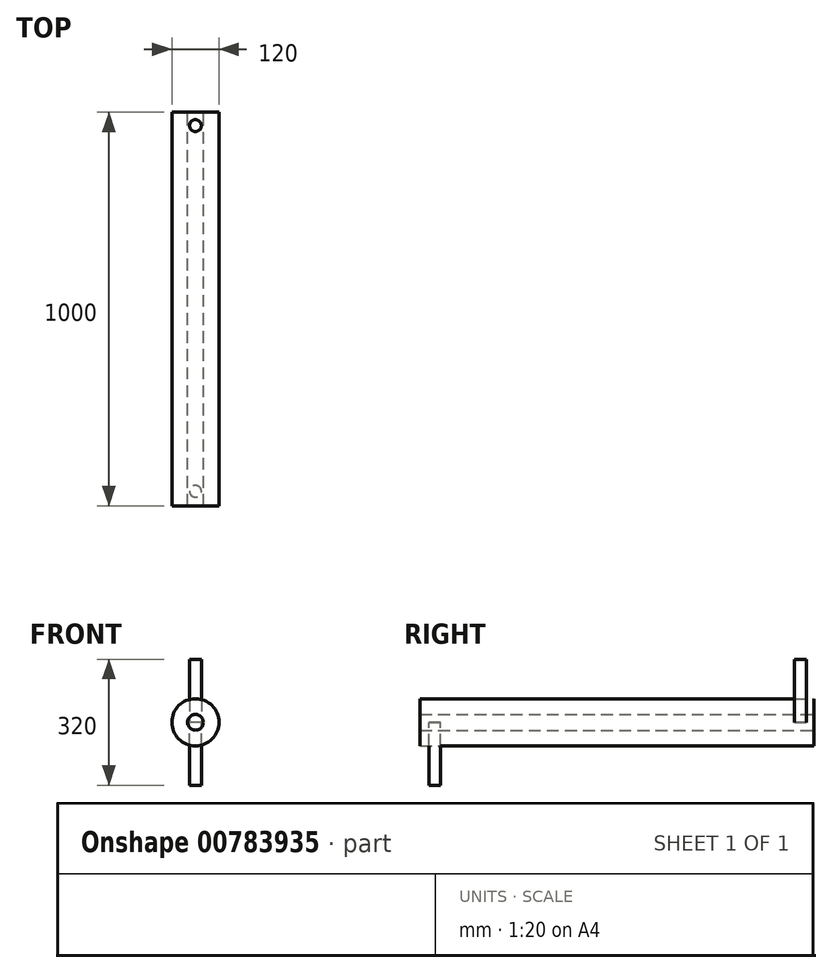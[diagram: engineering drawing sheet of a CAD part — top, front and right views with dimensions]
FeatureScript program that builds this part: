
annotation { "Feature Type Name" : "Feature", "Feature Type Description" : "" }
export const myFeature = defineFeature(function(context is Context, id is Id, definition is map)
    precondition{}
    {
        {
            var Q0;
            Q0=qCreatedBy(makeId("Front.planeOp"),FACE);
            var sketch = newSketch(context, id + "F0", { "sketchPlane" : qUnion([Q0])});
            skCircle(sketch, "E0", {"center": v(0, 0) * mm, "radius": 60 * mm});
            skSolve(sketch);
        }
        {
            var Q0;
            Q0=qCreatedBy(makeId("Front.planeOp"),FACE);
            var sketch = newSketch(context, id + "F1", { "sketchPlane" : qUnion([Q0])});
            skCircle(sketch, "E1", {"center": v(0, 0) * mm, "radius": 20 * mm});
            skSolve(sketch);
        }
        {
            var Q0;
            Q0=makeQuery(id+"F0.imprint","IMPRINT",FACE,{"disambiguationData":[TD([[makeQuery(id+"F0.imprint","IMPRINT",EDGE,{"derivedFrom":sQuery(id+"F0.wireOp",EDGE,"E0")}),1.0]])]});
            var Q1;
            Q1=makeQuery(id+"F1.imprint","IMPRINT",FACE,{"disambiguationData":[TD([[makeQuery(id+"F1.imprint","IMPRINT",EDGE,{"derivedFrom":sQuery(id+"F1.wireOp",EDGE,"E1")}),1.0]])]});
            extrude(context, id + "F2", {"entities" : qUnion([Q0, Q1]), "depth" : 1000 * mm, "offsetDistance" : 25 * mm});
        }
        {
            var Q0;
            Q0=qCreatedBy(makeId("Top.planeOp"),FACE);
            var sketch = newSketch(context, id + "F3", { "sketchPlane" : qUnion([Q0])});
            skCircle(sketch, "E2", {"center": v(0, -33.89) * mm, "radius": 15 * mm});
            skSolve(sketch);
        }
        {
            var Q0;
            Q0 = qSketchRegion(id + "F3", true);
            extrude(context, id + "F4", {"entities" : qUnion([Q0]), "depth" : 160 * mm, "offsetDistance" : 25 * mm});
        }
        {
            var Q0;
            Q0=qCreatedBy(makeId("Top.planeOp"),FACE);
            var sketch = newSketch(context, id + "F5", { "sketchPlane" : qUnion([Q0])});
            skCircle(sketch, "E3", {"center": v(0, -962.96) * mm, "radius": 15 * mm});
            skSolve(sketch);
        }
        {
            var Q0;
            Q0 = qSketchRegion(id + "F5", true);
            extrude(context, id + "F6", {"entities" : qUnion([Q0]), "oppositeDirection" : true, "depth" : 160 * mm, "offsetDistance" : 25 * mm});
        }
    });
